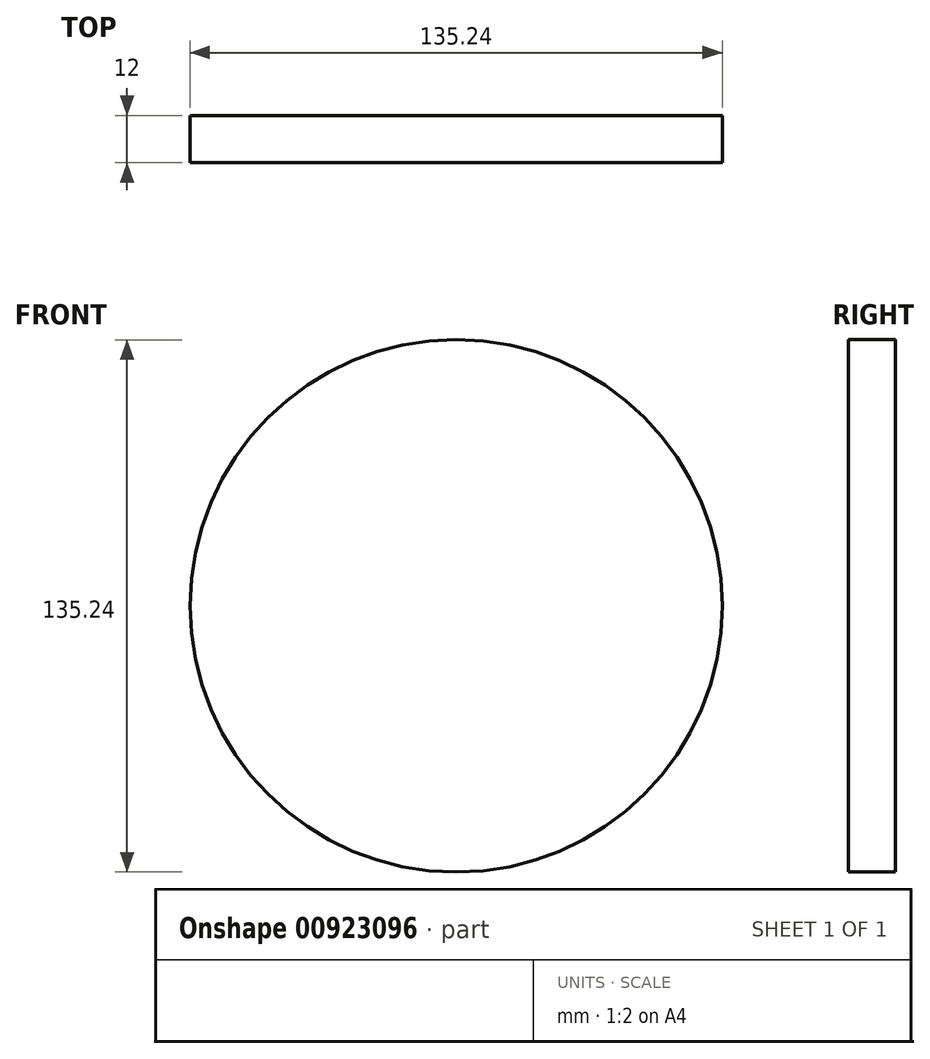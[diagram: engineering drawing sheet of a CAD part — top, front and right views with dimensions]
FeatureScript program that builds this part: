
annotation { "Feature Type Name" : "Feature", "Feature Type Description" : "" }
export const myFeature = defineFeature(function(context is Context, id is Id, definition is map)
    precondition{}
    {
        {
            var Q0;
            Q0=qCreatedBy(makeId("Front.planeOp"),FACE);
            var sketch = newSketch(context, id + "F0", { "sketchPlane" : qUnion([Q0])});
            skCircle(sketch, "E0", {"center": v(0, 0) * mm, "radius": 67.62 * mm});
            skSolve(sketch);
        }
        {
            var Q0;
            Q0=sQuery(id+"F0.wireOp",EDGE,"E0");
            extrude(context, id + "F1", {"bodyType" : ToolBodyType.SURFACE, "surfaceEntities" : qUnion([Q0]), "depth" : 12 * mm, "offsetDistance" : 25 * mm});
        }
    });
